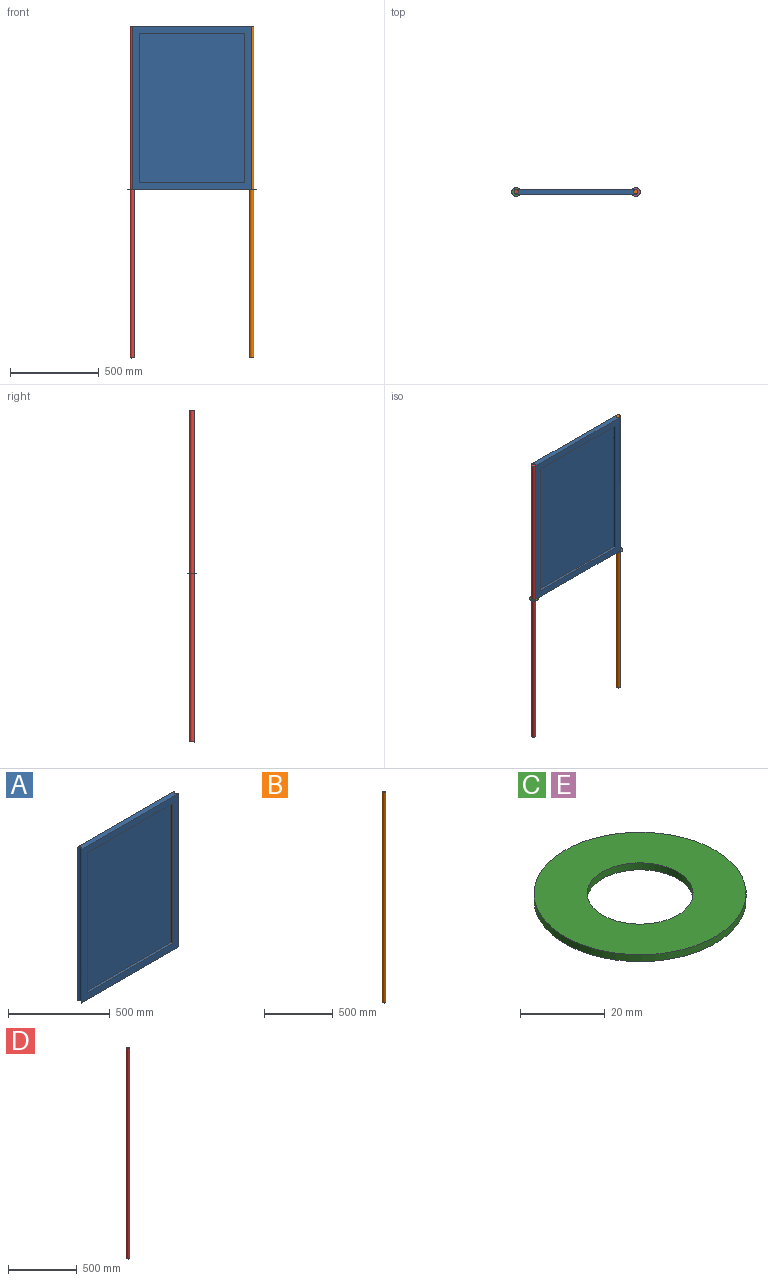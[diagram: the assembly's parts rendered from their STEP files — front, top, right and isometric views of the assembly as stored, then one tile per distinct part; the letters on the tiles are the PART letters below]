
ASSEMBLY  parts=5 mates=4
PART A: 15 faces, bbox 674x30x921 mm
  f0: plane 921x2.5mm, normal (-1,0,0), area 2302.5mm2, adj f3,f5,f7,f14
  f1: plane 921x2.5mm, normal (1,0,0), area 2302.5mm2, adj f3,f5,f7,f13
  f2: plane 921x674mm, normal (0,-1,0), area 121200mm2, adj f3,f4,f5,f6,f8,f9,f10,f11
  f3: plane 674x30mm, normal (0,0,1), area 19729.1mm2, adj f0,f1,f2,f4,f6,f7,f13,f14
  f4: plane 921x2.5mm, normal (-1,0,0), area 2302.5mm2, adj f2,f3,f5,f14
  f5: plane 674x30mm, normal (0,0,-1), area 19729.1mm2, adj f0,f1,f2,f4,f6,f7,f13,f14
  f6: plane 921x2.5mm, normal (1,0,0), area 2302.5mm2, adj f2,f3,f5,f13
  f7: plane 921x674mm, normal (0,1,0), area 620754mm2, adj f0,f1,f3,f5
  f8: plane 594x15mm, normal (0,0,-1), area 8910mm2, adj f2,f9,f11,f12
  f9: plane 841x15mm, normal (1,0,0), area 12615mm2, adj f2,f8,f10,f12
  f10: plane 594x15mm, normal (0,0,1), area 8910mm2, adj f2,f9,f11,f12
  f11: plane 841x15mm, normal (-1,0,0), area 12615mm2, adj f2,f8,f10,f12
  f12: plane 841x594mm, normal (0,-1,0), area 499554mm2, adj f8,f9,f10,f11
  f13: cylinder r=12.5mm len=921mm, axis (0,0,1), area 36167.6mm2, adj f1,f3,f5,f6
  f14: cylinder r=12.5mm len=921mm, axis (0,0,1), area 36167.6mm2, adj f0,f3,f4,f5
PART B: 3 faces, bbox 25x25x1869 mm
  f0: cylinder r=12.5mm len=1869mm, axis (0,0,-1), area 146790.9mm2, adj f1,f2
  f1: plane 25x25mm, normal (0,0,1), area 490.9mm2, adj f0
  f2: plane 25x25mm, normal (0,0,-1), area 490.9mm2, adj f0
PART C: 4 faces, bbox 50x50x2 mm
  f0: cylinder r=12.5mm len=25mm, axis (0,0,-1), area 157.1mm2, adj f2,f3
  f1: cylinder r=25mm len=50mm, axis (0,0,-1), area 314.2mm2, adj f2,f3
  f2: plane 50x50mm, normal (0,0,1), area 1472.6mm2, adj f0,f1
  f3: plane 50x50mm, normal (0,0,-1), area 1472.6mm2, adj f0,f1
PART D: 3 faces, bbox 25x25x1869 mm
  f0: cylinder r=12.5mm len=1869mm, axis (0,0,-1), area 146790.9mm2, adj f1,f2
  f1: plane 25x25mm, normal (0,0,1), area 490.9mm2, adj f0
  f2: plane 25x25mm, normal (0,0,-1), area 490.9mm2, adj f0
PART E: same geometry as C
PLACE A t=(-121.54,113.05,-515.79)mm
PLACE B t=(-16.72,98.05,-1836.16)mm
PLACE C t=(-454.96,98.05,-891.31)mm
PLACE D t=(-265.54,98.05,-1838.93)mm
PLACE E t=(219.04,98.05,-891.39)mm
MATE cylindrical A.f13 <-> B.f0  axis (0,0,1) through (219.04,98.05,-428.85)mm
MATE cylindrical D.f0 <-> C.f0  axis (0,0,-1) through (-454.96,98.05,-904.43)mm
MATE cylindrical A.f14 <-> D.f0  axis (0,0,1) through (-454.96,98.05,-428.85)mm
MATE cylindrical B.f0 <-> E.f0  axis (0,0,-1) through (219.04,98.05,-901.66)mm
